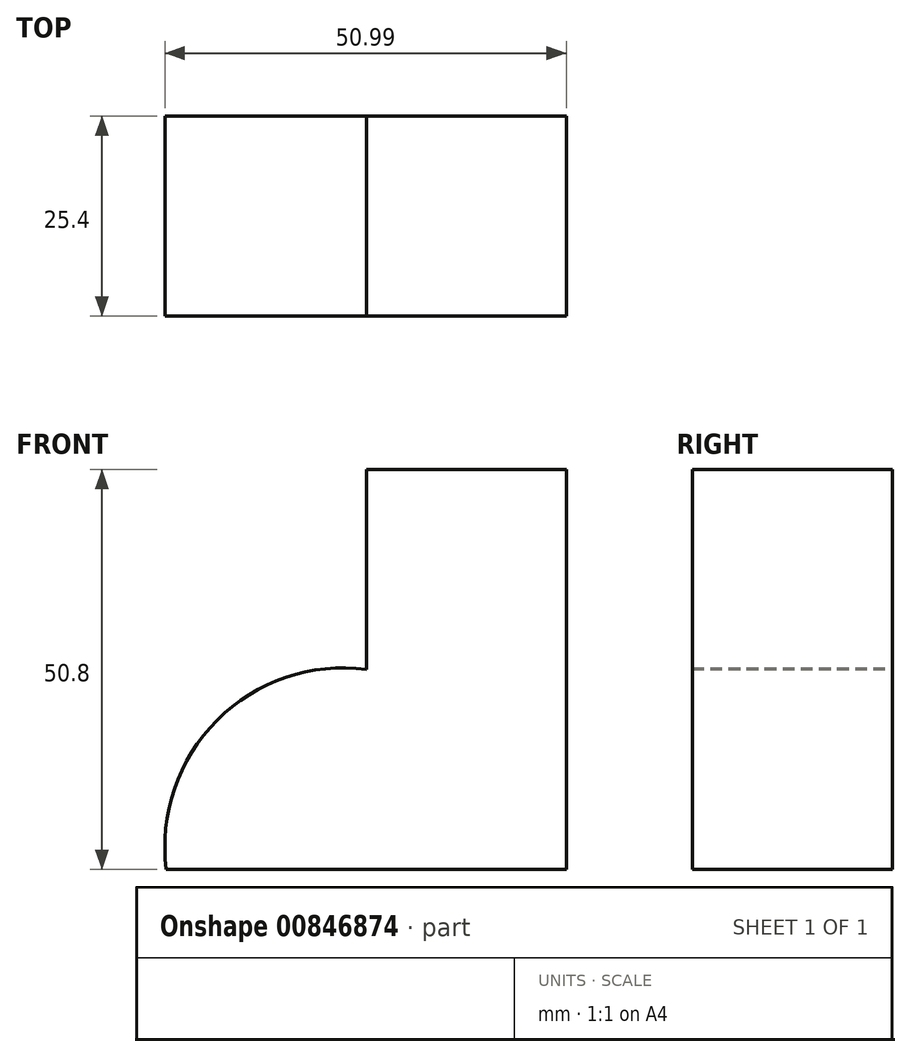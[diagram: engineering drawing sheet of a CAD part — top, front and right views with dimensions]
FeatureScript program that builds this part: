
annotation { "Feature Type Name" : "Feature", "Feature Type Description" : "" }
export const myFeature = defineFeature(function(context is Context, id is Id, definition is map)
    precondition{}
    {
        {
            var Q0;
            Q0=qCreatedBy(makeId("Front.planeOp"),FACE);
            var sketch = newSketch(context, id + "F0", { "sketchPlane" : qUnion([Q0])});
            skLineSegment(sketch, "E0", {"start": v(0, 0) * mm, "end": v(50.8, 0) * mm});
            skLineSegment(sketch, "E1", {"start": v(50.8, 0) * mm, "end": v(50.8, 50.8) * mm});
            skLineSegment(sketch, "E2", {"start": v(50.8, 50.8) * mm, "end": v(25.4, 50.8) * mm});
            skLineSegment(sketch, "E3", {"start": v(25.4, 50.8) * mm, "end": v(25.4, 25.4) * mm});
            skArc(sketch, "E4", {"start": v(25.4, 25.4) * mm, "mid": v(6.45, 18.95) * mm, "end": v(0, 0) * mm});
            skSolve(sketch);
        }
        {
            var Q0;
            Q0=qSketchRegion(id+"F0",true);
            extrude(context, id + "F1", {"entities" : qUnion([Q0]), "depth" : 25.4 * mm, "offsetDistance" : 25.4 * mm});
        }
    });
